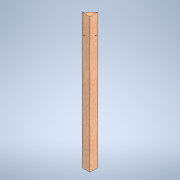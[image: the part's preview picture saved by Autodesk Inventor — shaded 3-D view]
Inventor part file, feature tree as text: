
AUTODESK INVENTOR PART (.ipt)
format: ipt  version: 2022 (Build 260153000, 153)  size: 113,152 bytes
history: native  units: mm
features: sketch x2, other x1, extrude x1, hole x1
ambient origin geometry x8: Origin, YZ Plane, XZ Plane, XY Plane, X Axis, Y Axis, Z Axis, Center Point
bodies: Body1 (feature_tree)
feature tree (5):
  other  "Sólido1"
  extrude  "Extrusão1"  Depth=700.0mm
  hole  "Furo1"  [1 undecoded]
  sketch  "Esboço1"  dims[d2=700.0mm d3=0.0mm d4=100.0mm]
  sketch  "Esboço2"  dims[d5=21.5mm d6=21.5mm d7=3.0mm d8=6.0mm d9=4.0mm d10=2.0mm d11=90.0deg d12=8.0mm d13=20.594885mm]
note: 1 required parameter value undecoded (feature->parameter linkage not recoverable at this tier; creation-order binding heuristic only, values carry confidence <= 0.55)
